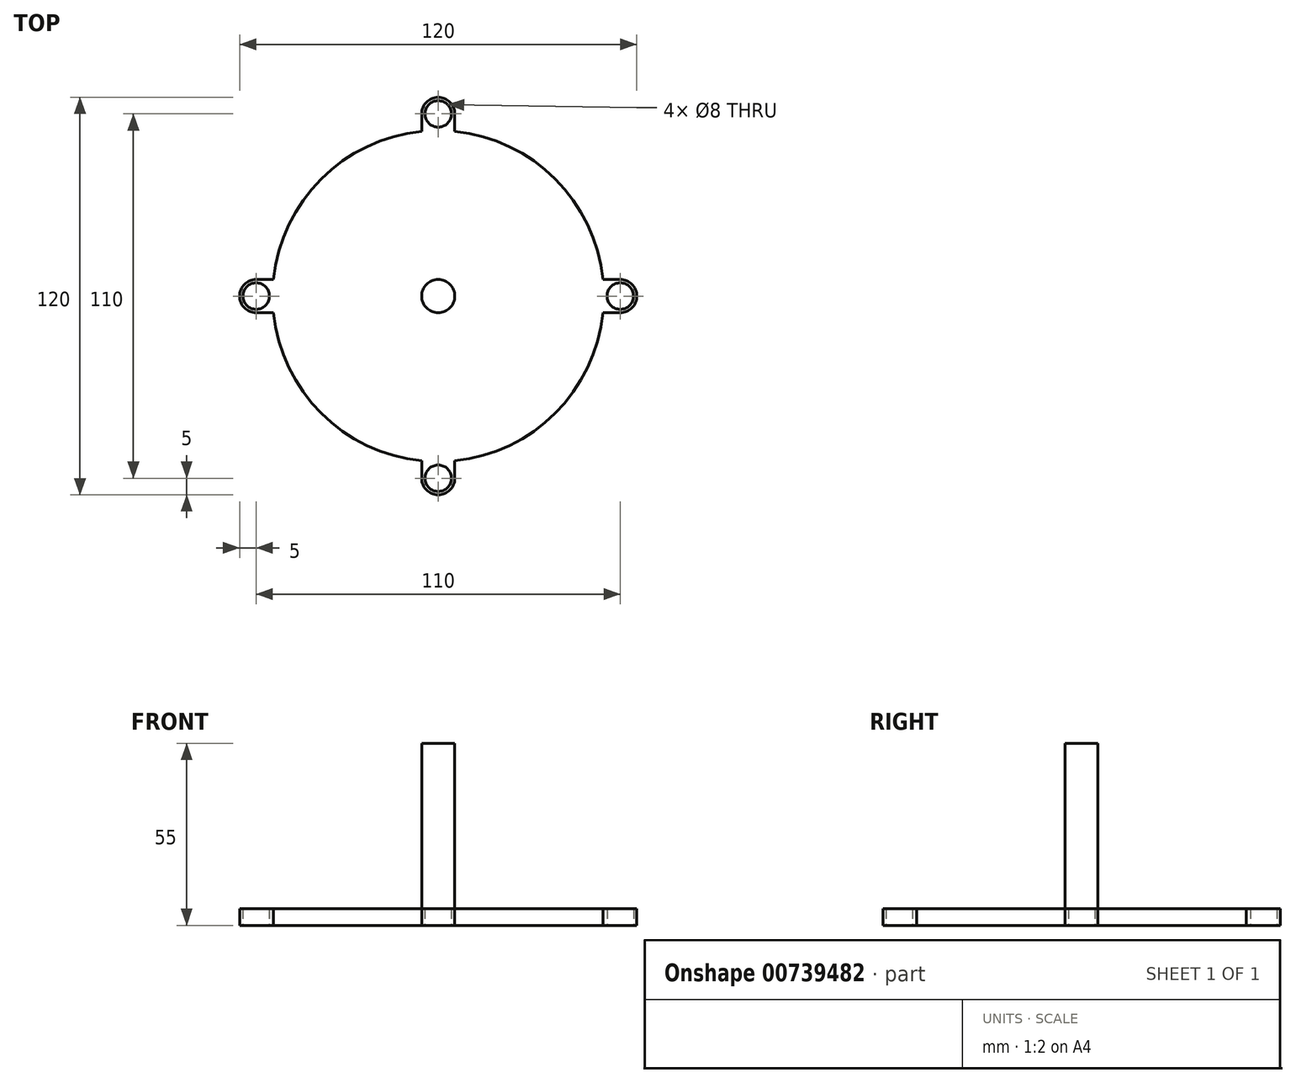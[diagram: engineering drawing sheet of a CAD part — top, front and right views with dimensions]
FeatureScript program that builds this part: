
annotation { "Feature Type Name" : "Feature", "Feature Type Description" : "" }
export const myFeature = defineFeature(function(context is Context, id is Id, definition is map)
    precondition{}
    {
        {
            var Q0;
            Q0=qCreatedBy(makeId("Top.planeOp"),FACE);
            var sketch = newSketch(context, id + "F0", { "sketchPlane" : qUnion([Q0])});
            skCircle(sketch, "E0", {"center": v(0, 0) * mm, "radius": 50 * mm});
            skLineSegment(sketch, "E1", {"start": v(0, 0) * mm, "end": v(0, 55) * mm});
            skCircle(sketch, "E2", {"center": v(0, 55) * mm, "radius": 5 * mm});
            skLineSegment(sketch, "E3", {"start": v(5, 55) * mm, "end": v(5, 49.75) * mm});
            skLineSegment(sketch, "E4", {"start": v(-5, 55) * mm, "end": v(-5, 49.75) * mm});
            skCircle(sketch, "E5.1.0", {"center": v(-55, 0) * mm, "radius": 5 * mm});
            skLineSegment(sketch, "E5.1.1", {"start": v(-55, 5) * mm, "end": v(-49.75, 5) * mm});
            skLineSegment(sketch, "E5.1.2", {"start": v(-55, -5) * mm, "end": v(-49.75, -5) * mm});
            skCircle(sketch, "E5.2.0", {"center": v(0, -55) * mm, "radius": 5 * mm});
            skLineSegment(sketch, "E5.2.1", {"start": v(-5, -55) * mm, "end": v(-5, -49.75) * mm});
            skLineSegment(sketch, "E5.2.2", {"start": v(5, -55) * mm, "end": v(5, -49.75) * mm});
            skCircle(sketch, "E5.3.0", {"center": v(55, 0) * mm, "radius": 5 * mm});
            skLineSegment(sketch, "E5.3.1", {"start": v(55, -5) * mm, "end": v(49.75, -5) * mm});
            skLineSegment(sketch, "E5.3.2", {"start": v(55, 5) * mm, "end": v(49.75, 5) * mm});
            skCircle(sketch, "E6", {"center": v(0, 55) * mm, "radius": 4 * mm});
            skCircle(sketch, "E7.1.0", {"center": v(-55, 0) * mm, "radius": 4 * mm});
            skCircle(sketch, "E7.2.0", {"center": v(0, -55) * mm, "radius": 4 * mm});
            skCircle(sketch, "E7.3.0", {"center": v(55, 0) * mm, "radius": 4 * mm});
            skSolve(sketch);
        }
        {
            var Q0;
            Q0=makeQuery(id+"F0.imprint","IMPRINT",FACE,{"disambiguationData":[TD([[makeQuery(id+"F0.imprint","IMPRINT",EDGE,{"derivedFrom":sQuery(id+"F0.wireOp",EDGE,"E0")}),1.0]])]});
            var Q1;
            Q1=makeQuery(id+"F0.imprint","IMPRINT",FACE,{"disambiguationData":[TD([[makeQuery(id+"F0.imprint","IMPRINT",EDGE,{"derivedFrom":sQuery(id+"F0.wireOp",EDGE,"E6")}),-1.0]])]});
            var Q2;
            {var subQ0=sQuery(id+"F0.wireOp",EDGE,"E4");Q2=makeQuery(id+"F0.imprint","IMPRINT",FACE,{"disambiguationData":[TD([[makeQuery(id+"F0.imprint","IMPRINT",EDGE,{"derivedFrom":subQ0}),1.0]])]});}
            var Q3;
            {var subQ0=sQuery(id+"F0.wireOp",EDGE,"E3");Q3=makeQuery(id+"F0.imprint","IMPRINT",FACE,{"disambiguationData":[TD([[makeQuery(id+"F0.imprint","IMPRINT",EDGE,{"derivedFrom":subQ0}),-1.0]])]});}
            var Q4;
            Q4=makeQuery(id+"F0.imprint","IMPRINT",FACE,{"disambiguationData":[TD([[makeQuery(id+"F0.imprint","IMPRINT",EDGE,{"derivedFrom":sQuery(id+"F0.wireOp",EDGE,"E7.3.0")}),-1.0]])]});
            var Q5;
            {var subQ0=sQuery(id+"F0.wireOp",EDGE,"E5.3.1");Q5=makeQuery(id+"F0.imprint","IMPRINT",FACE,{"disambiguationData":[TD([[makeQuery(id+"F0.imprint","IMPRINT",EDGE,{"derivedFrom":subQ0}),-1.0]])]});}
            var Q6;
            {var subQ0=sQuery(id+"F0.wireOp",EDGE,"E5.3.2");Q6=makeQuery(id+"F0.imprint","IMPRINT",FACE,{"disambiguationData":[TD([[makeQuery(id+"F0.imprint","IMPRINT",EDGE,{"derivedFrom":subQ0}),1.0]])]});}
            var Q7;
            {var subQ0=sQuery(id+"F0.wireOp",EDGE,"E5.2.2");Q7=makeQuery(id+"F0.imprint","IMPRINT",FACE,{"disambiguationData":[TD([[makeQuery(id+"F0.imprint","IMPRINT",EDGE,{"derivedFrom":subQ0}),1.0]])]});}
            var Q8;
            {var subQ0=sQuery(id+"F0.wireOp",EDGE,"E5.2.1");Q8=makeQuery(id+"F0.imprint","IMPRINT",FACE,{"disambiguationData":[TD([[makeQuery(id+"F0.imprint","IMPRINT",EDGE,{"derivedFrom":subQ0}),-1.0]])]});}
            var Q9;
            Q9=makeQuery(id+"F0.imprint","IMPRINT",FACE,{"disambiguationData":[TD([[makeQuery(id+"F0.imprint","IMPRINT",EDGE,{"derivedFrom":sQuery(id+"F0.wireOp",EDGE,"E7.2.0")}),-1.0]])]});
            var Q10;
            Q10=makeQuery(id+"F0.imprint","IMPRINT",FACE,{"disambiguationData":[TD([[makeQuery(id+"F0.imprint","IMPRINT",EDGE,{"derivedFrom":sQuery(id+"F0.wireOp",EDGE,"E7.1.0")}),-1.0]])]});
            var Q11;
            {var subQ0=sQuery(id+"F0.wireOp",EDGE,"E5.1.2");Q11=makeQuery(id+"F0.imprint","IMPRINT",FACE,{"disambiguationData":[TD([[makeQuery(id+"F0.imprint","IMPRINT",EDGE,{"derivedFrom":subQ0}),1.0]])]});}
            var Q12;
            {var subQ0=sQuery(id+"F0.wireOp",EDGE,"E5.1.1");Q12=makeQuery(id+"F0.imprint","IMPRINT",FACE,{"disambiguationData":[TD([[makeQuery(id+"F0.imprint","IMPRINT",EDGE,{"derivedFrom":subQ0}),-1.0]])]});}
            extrude(context, id + "F1", {"entities" : qUnion([Q0, Q1, Q2, Q3, Q4, Q5, Q6, Q7, Q8, Q9, Q10, Q11, Q12]), "endBound" : BoundingType.SYMMETRIC, "depth" : 5 * mm, "offsetDistance" : 25 * mm});
        }
        {
            var Q0;
            Q0=makeQuery(id+"F1.opExtrude","CAP_FACE",FACE,{"disambiguationData":[OSD([sQuery(id+"F0.wireOp",EDGE,"E0")])],"isStart":false});
            var sketch = newSketch(context, id + "F2", { "sketchPlane" : qUnion([Q0])});
            skCircle(sketch, "E8", {"center": v(0, 0) * mm, "radius": 5 * mm});
            skSolve(sketch);
        }
        {
            var Q0;
            Q0 = qSketchRegion(id + "F2", true);
            extrude(context, id + "F3", {"entities" : qUnion([Q0]), "operationType" : NewBodyOperationType.ADD, "depth" : 50 * mm, "offsetDistance" : 25 * mm});
        }
    });
